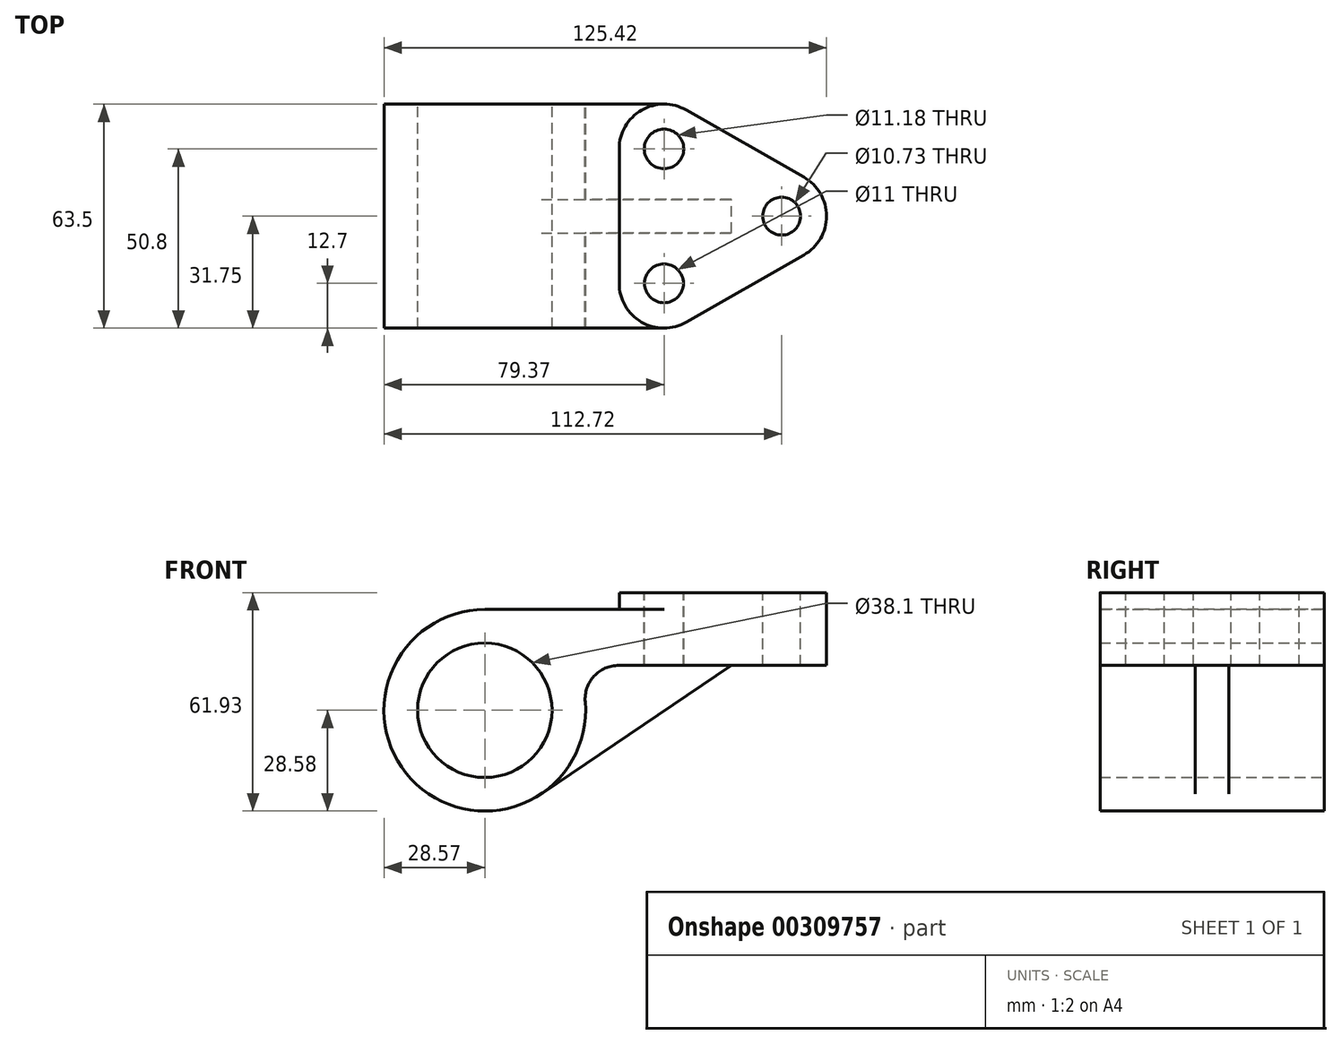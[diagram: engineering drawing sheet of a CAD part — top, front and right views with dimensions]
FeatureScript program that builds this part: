
annotation { "Feature Type Name" : "Feature", "Feature Type Description" : "" }
export const myFeature = defineFeature(function(context is Context, id is Id, definition is map)
    precondition{}
    {
        {
            var Q0;
            Q0=qCreatedBy(makeId("Front.planeOp"),FACE);
            var sketch = newSketch(context, id + "F0", { "sketchPlane" : qUnion([Q0])});
            skArc(sketch, "E0", {"start": v(0, 28.58) * mm, "mid": v(-19.34, -21.04) * mm, "end": v(28.47, 2.4) * mm});
            skCircle(sketch, "E1", {"center": v(0, 0) * mm, "radius": 19.05 * mm});
            skLineSegment(sketch, "E2", {"start": v(0, 28.58) * mm, "end": v(96.85, 28.58) * mm});
            skArc(sketch, "E3", {"start": v(37.97, 12.72) * mm, "mid": v(30.95, 9.64) * mm, "end": v(28.47, 2.4) * mm});
            skLineSegment(sketch, "E4", {"start": v(37.97, 12.72) * mm, "end": v(96.85, 12.72) * mm});
            skLineSegment(sketch, "E5", {"start": v(96.85, 12.72) * mm, "end": v(96.85, 28.58) * mm});
            skSolve(sketch);
        }
        {
            var Q0;
            Q0 = qSketchRegion(id + "F0", true);
            extrude(context, id + "F1", {"entities" : qUnion([Q0]), "endBound" : BoundingType.SYMMETRIC, "depth" : 63.5 * mm});
        }
        {
            var Q0;
            Q0=makeQuery(id+"F1.opExtrude","SWEPT_FACE",FACE,{"disambiguationData":[OSD([sQuery(id+"F0.wireOp",EDGE,"E2")])]});
            var sketch = newSketch(context, id + "F2", { "sketchPlane" : qUnion([Q0])});
            skArc(sketch, "E6", {"start": v(57.1, 30.08) * mm, "mid": v(44.42, 30.03) * mm, "end": v(38.1, 19.05) * mm});
            skArc(sketch, "E7", {"start": v(38.1, -19.05) * mm, "mid": v(44.42, -30.03) * mm, "end": v(57.1, -30.08) * mm});
            skArc(sketch, "E8", {"start": v(90.45, -11.03) * mm, "mid": v(96.85, 0) * mm, "end": v(90.45, 11.03) * mm});
            skPoint(sketch, "E8.centerSnap0", {"position": v(96.85, 0) * mm});
            skLineSegment(sketch, "E9", {"start": v(90.45, -11.03) * mm, "end": v(57.1, -30.08) * mm});
            skLineSegment(sketch, "E10", {"start": v(38.1, 19.05) * mm, "end": v(38.1, -19.05) * mm});
            skLineSegment(sketch, "E11", {"start": v(57.1, 30.08) * mm, "end": v(90.45, 11.03) * mm});
            skSolve(sketch);
        }
        {
            var Q0;
            Q0 = qSketchRegion(id + "F2", true);
            extrude(context, id + "F3", {"entities" : qUnion([Q0]), "operationType" : NewBodyOperationType.ADD, "depth" : 4.78 * mm});
        }
        {
            var Q0;
            Q0=makeQuery(id+"F3.opExtrude","CAP_FACE",FACE,{"disambiguationData":[OSD([sQuery(id+"F2.wireOp",EDGE,"E6"),sQuery(id+"F2.wireOp",EDGE,"E7"),sQuery(id+"F2.wireOp",EDGE,"E8"),sQuery(id+"F2.wireOp",EDGE,"E9"),sQuery(id+"F2.wireOp",EDGE,"E10"),sQuery(id+"F2.wireOp",EDGE,"E11")])],"isStart":false});
            var sketch = newSketch(context, id + "F4", { "sketchPlane" : qUnion([Q0])});
            skCircle(sketch, "E12", {"center": v(50.8, 19.05) * mm, "radius": 5.6 * mm});
            skCircle(sketch, "E13", {"center": v(50.8, -19.05) * mm, "radius": 5.5 * mm});
            skCircle(sketch, "E14", {"center": v(84.15, 0) * mm, "radius": 5.37 * mm});
            skArc(sketch, "E15.0", {"start": v(57.1, 30.08) * mm, "mid": v(54.06, 31.32) * mm, "end": v(50.8, 31.75) * mm});
            skArc(sketch, "E16.0", {"start": v(90.45, -11.03) * mm, "mid": v(96.85, 0) * mm, "end": v(90.45, 11.03) * mm});
            skArc(sketch, "E17.0", {"start": v(50.8, -31.75) * mm, "mid": v(54.06, -31.32) * mm, "end": v(57.1, -30.08) * mm});
            skLineSegment(sketch, "E18.0", {"start": v(57.1, 30.08) * mm, "end": v(90.45, 11.03) * mm});
            skLineSegment(sketch, "E19.0", {"start": v(90.45, -11.03) * mm, "end": v(57.1, -30.08) * mm});
            skPoint(sketch, "E20.0", {"position": v(38.1, 0) * mm});
            skLineSegment(sketch, "E21", {"start": v(50.8, -31.75) * mm, "end": v(50.8, -39.86) * mm});
            skLineSegment(sketch, "E22", {"start": v(50.8, -39.86) * mm, "end": v(111.59, -39.86) * mm});
            skLineSegment(sketch, "E23", {"start": v(111.59, -39.86) * mm, "end": v(111.59, 45.15) * mm});
            skLineSegment(sketch, "E24", {"start": v(111.59, 45.15) * mm, "end": v(50.8, 45.15) * mm});
            skLineSegment(sketch, "E25", {"start": v(50.8, 45.15) * mm, "end": v(50.8, 31.75) * mm});
            skPoint(sketch, "E26.orphan", {"position": v(38.1, 19.05) * mm});
            skPoint(sketch, "E27.orphan", {"position": v(38.1, -19.05) * mm});
            skSolve(sketch);
        }
        {
            var Q0;
            Q0 = qSketchRegion(id + "F4", true);
            extrude(context, id + "F5", {"entities" : qUnion([Q0]), "operationType" : NewBodyOperationType.REMOVE, "endBound" : BoundingType.THROUGH_ALL, "oppositeDirection" : true, "depth" : 25.4 * mm});
        }
        {
            var Q0;
            Q0=qCreatedBy(makeId("Front.planeOp"),FACE);
            var sketch = newSketch(context, id + "F6", { "sketchPlane" : qUnion([Q0])});
            skArc(sketch, "E28.0", {"start": v(0, 28.58) * mm, "mid": v(-19.34, -21.04) * mm, "end": v(28.47, 2.4) * mm});
            skLineSegment(sketch, "E29.0", {"start": v(90.45, 12.72) * mm, "end": v(57.1, 12.72) * mm});
            skArc(sketch, "E30.0", {"start": v(37.97, 12.72) * mm, "mid": v(30.95, 9.64) * mm, "end": v(28.47, 2.4) * mm});
            skLineSegment(sketch, "E31.0", {"start": v(37.97, 12.72) * mm, "end": v(50.8, 12.72) * mm});
            skLineSegment(sketch, "E32.0", {"start": v(50.8, 12.72) * mm, "end": v(57.1, 12.72) * mm});
            skLineSegment(sketch, "E33", {"start": v(16, -23.68) * mm, "end": v(69.85, 12.72) * mm});
            skSolve(sketch);
        }
        {
            var Q0;
            Q0 = qSketchRegion(id + "F6", true);
            extrude(context, id + "F7", {"entities" : qUnion([Q0]), "operationType" : NewBodyOperationType.ADD, "endBound" : BoundingType.SYMMETRIC, "depth" : 9.52 * mm});
        }
    });
